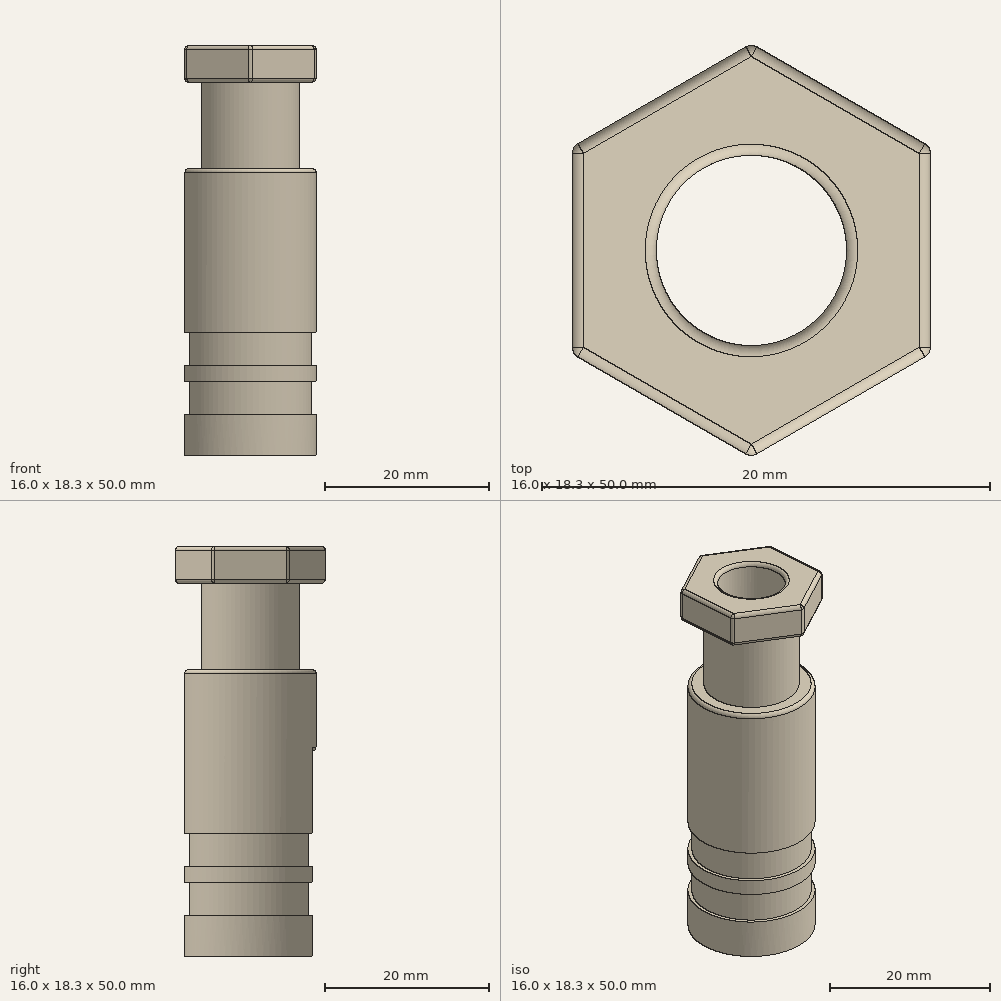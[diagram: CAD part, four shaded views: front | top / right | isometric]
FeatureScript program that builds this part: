
annotation { "Feature Type Name" : "Feature", "Feature Type Description" : "" }
export const myFeature = defineFeature(function(context is Context, id is Id, definition is map)
    precondition{}
    {
        {
            assignVariable(context, id + "F0", {"name" : "Sensor_Laenge", "anyValue" : 25});
        }
        {
            assignVariable(context, id + "F1", {"name" : "Hoehe_Mutter", "anyValue" : 4.5});
        }
        {
            assignVariable(context, id + "F2", {"name" : "Hoehe_Verlaengerung", "anyValue" : 15});
        }
        {
            var Q0;
            Q0=qCreatedBy(makeId("Top.planeOp"),FACE);
            var sketch = newSketch(context, id + "F3", { "sketchPlane" : qUnion([Q0])});
            skLineSegment(sketch, "E0", {"start": v(-2.5, 7.6) * mm, "end": v(-2.5, 3.44) * mm});
            skLineSegment(sketch, "E1", {"start": v(2.5, 7.6) * mm, "end": v(2.5, 3.44) * mm});
            skCircle(sketch, "E2", {"center": v(0, 0) * mm, "radius": 4.25 * mm});
            skCircle(sketch, "E3", {"center": v(0, 0) * mm, "radius": 8 * mm});
            skLineSegment(sketch, "E4", {"start": v(0, 0) * mm, "end": v(0, 8) * mm, "construction": true});
            skCircle(sketch, "E5", {"center": v(0, 0) * mm, "radius": 7.5 * mm});
            skSolve(sketch);
        }
        {
            var Q0;
            {var subQ0=sQuery(id+"F3.wireOp",EDGE,"E2");var subQ1=sQuery(id+"F3.wireOp",EDGE,"E0");var subQ2=makeQuery(id+"F3.imprint","INTERSECT",VERTEX,{"derivedFrom":[subQ1,subQ0]});Q0=makeQuery(id+"F3.imprint","IMPRINT",FACE,{"disambiguationData":[TD([[makeQuery(id+"F3.imprint","IMPRINT",EDGE,{"disambiguationData":[TD([[subQ2,1.0]])],"derivedFrom":subQ1}),-1.0]])]});}
            var Q1;
            {var subQ0=sQuery(id+"F3.wireOp",EDGE,"E3");var subQ1=sQuery(id+"F3.wireOp",EDGE,"E0");var subQ2=makeQuery(id+"F3.imprint","INTERSECT",VERTEX,{"derivedFrom":[subQ1,subQ0]});Q1=makeQuery(id+"F3.imprint","IMPRINT",FACE,{"disambiguationData":[TD([[makeQuery(id+"F3.imprint","IMPRINT",EDGE,{"disambiguationData":[TD([[subQ2,-1.0]])],"derivedFrom":subQ1}),-1.0]])]});}
            extrude(context, id + "F4", {"entities" : qUnion([Q0, Q1]), "oppositeDirection" : true, "depth" : (getVariable(context, 'Sensor_Laenge')) * mm, "offsetDistance" : 25 * mm});
        }
        {
            var Q0;
            {var subQ0=sQuery(id+"F3.wireOp",EDGE,"7UpqIU3J-aBD8-OsaK-lXAZ-pH7eXoIEcfKO.right");var subQ3=sQuery(id+"F3.wireOp",EDGE,"E2");var subQ4=makeQuery(id+"F3.imprint","INTERSECT",VERTEX,{"disambiguationData":[OD(0.0)],"derivedFrom":[subQ3,subQ0]});Q0=makeQuery(id+"F3.imprint","IMPRINT",FACE,{"disambiguationData":[TD([[makeQuery(id+"F3.imprint","IMPRINT",EDGE,{"disambiguationData":[TD([[subQ4,-1.0]])],"derivedFrom":subQ3}),-1.0]])]});}
            var Q1;
            {var subQ0=sQuery(id+"F3.wireOp",EDGE,"E1");Q1=makeQuery(id+"F3.imprint","IMPRINT",FACE,{"disambiguationData":[TD([[makeQuery(id+"F3.imprint","IMPRINT",EDGE,{"derivedFrom":subQ0}),1.0]])]});}
            var Q2;
            {var subQ0=sQuery(id+"F3.wireOp",EDGE,"E1");Q2=makeQuery(id+"F3.imprint","IMPRINT",FACE,{"disambiguationData":[TD([[makeQuery(id+"F3.imprint","IMPRINT",EDGE,{"derivedFrom":subQ0}),-1.0]])]});}
            extrude(context, id + "F5", {"entities" : qUnion([Q0, Q1, Q2]), "operationType" : NewBodyOperationType.ADD, "depth" : 10 * mm, "offsetDistance" : 25 * mm});
        }
        {
            var Q0;
            {var subQ0=sQuery(id+"F3.wireOp",EDGE,"E3");var subQ1=sQuery(id+"F3.wireOp",EDGE,"E0");var subQ2=makeQuery(id+"F3.imprint","INTERSECT",VERTEX,{"derivedFrom":[subQ1,subQ0]});Q0=makeQuery(id+"F3.imprint","IMPRINT",FACE,{"disambiguationData":[TD([[makeQuery(id+"F3.imprint","IMPRINT",EDGE,{"disambiguationData":[TD([[subQ2,-1.0]])],"derivedFrom":subQ1}),-1.0]])]});}
            extrude(context, id + "F6", {"entities" : qUnion([Q0]), "operationType" : NewBodyOperationType.REMOVE, "oppositeDirection" : true, "depth" : 14 * mm, "offsetDistance" : 25 * mm, "hasSecondDirection" : true, "secondDirectionOppositeDirection" : true, "secondDirectionDepth" : 10 * mm});
        }
        {
            var Q0;
            {var subQ0=sQuery(id+"F3.wireOp",EDGE,"E3");var subQ1=sQuery(id+"F3.wireOp",EDGE,"E0");var subQ2=makeQuery(id+"F3.imprint","INTERSECT",VERTEX,{"derivedFrom":[subQ1,subQ0]});Q0=makeQuery(id+"F3.imprint","IMPRINT",FACE,{"disambiguationData":[TD([[makeQuery(id+"F3.imprint","IMPRINT",EDGE,{"disambiguationData":[TD([[subQ2,-1.0]])],"derivedFrom":subQ1}),-1.0]])]});}
            extrude(context, id + "F7", {"entities" : qUnion([Q0]), "operationType" : NewBodyOperationType.REMOVE, "oppositeDirection" : true, "depth" : 20 * mm, "offsetDistance" : 25 * mm, "hasSecondDirection" : true, "secondDirectionOppositeDirection" : true, "secondDirectionDepth" : 16 * mm});
        }
        {
            var Q0;
            Q0=makeQuery(id+"F5.opExtrude","CAP_FACE",FACE,{"disambiguationData":[OSD([sQuery(id+"F3.wireOp",EDGE,"E3"),sQuery(id+"F3.wireOp",EDGE,"WfVQaAh2-LhFR-lcju-hiQk-xBlA84VSb2D0")])],"isStart":false});
            var sketch = newSketch(context, id + "F8", { "sketchPlane" : qUnion([Q0]), "disableImprinting" : false});
            skCircle(sketch, "E6", {"center": v(0, 0) * mm, "radius": 6 * mm});
            skCircle(sketch, "E7", {"center": v(0, 0) * mm, "radius": 4.25 * mm});
            skSolve(sketch);
        }
        {
            var Q0;
            Q0=makeQuery(id+"F8.imprint","IMPRINT",FACE,{"disambiguationData":[TD([[makeQuery(id+"F8.imprint","IMPRINT",EDGE,{"derivedFrom":sQuery(id+"F8.wireOp",EDGE,"E6")}),1.0]])]});
            extrude(context, id + "F9", {"entities" : qUnion([Q0]), "operationType" : NewBodyOperationType.ADD, "depth" : (getVariable(context, 'Hoehe_Verlaengerung')) * mm, "offsetDistance" : 25 * mm});
        }
        {
            var Q0;
            Q0=makeQuery(id+"F9.opExtrude","CAP_FACE",FACE,{"disambiguationData":[OSD([sQuery(id+"F3.wireOp",EDGE,"WfVQaAh2-LhFR-lcju-hiQk-xBlA84VSb2D0"),sQuery(id+"F8.wireOp",EDGE,"E6")])],"isStart":false});
            var sketch = newSketch(context, id + "F10", { "sketchPlane" : qUnion([Q0])});
            skCircle(sketch, "E8", {"center": v(0, 0) * mm, "radius": 2.5 * mm});
            skCircle(sketch, "E9.cCircle", {"center": v(0, 0) * mm, "radius": 8 * mm, "construction": true});
            skLineSegment(sketch, "E9.0", {"start": v(8, 4.62) * mm, "end": v(8, -4.62) * mm});
            skLineSegment(sketch, "E9.1", {"start": v(8, -4.62) * mm, "end": v(0, -9.24) * mm});
            skLineSegment(sketch, "E9.2", {"start": v(0, -9.24) * mm, "end": v(-8, -4.62) * mm});
            skLineSegment(sketch, "E9.3", {"start": v(-8, -4.62) * mm, "end": v(-8, 4.62) * mm});
            skLineSegment(sketch, "E9.4", {"start": v(-8, 4.62) * mm, "end": v(0, 9.24) * mm});
            skLineSegment(sketch, "E9.5", {"start": v(0, 9.24) * mm, "end": v(8, 4.62) * mm});
            skPoint(sketch, "E9.0.midPoint", {"position": v(8, 0) * mm});
            skCircle(sketch, "E10", {"center": v(0, 0) * mm, "radius": 6 * mm});
            skSolve(sketch);
        }
        {
            var Q0;
            Q0=makeQuery(id+"F10.imprint","IMPRINT",FACE,{"disambiguationData":[TD([[makeQuery(id+"F10.imprint","IMPRINT",EDGE,{"derivedFrom":sQuery(id+"F10.wireOp",EDGE,"E9.0")}),-1.0]])]});
            extrude(context, id + "F11", {"entities" : qUnion([Q0]), "operationType" : NewBodyOperationType.ADD, "oppositeDirection" : true, "depth" : (getVariable(context, 'Hoehe_Mutter')) * mm, "offsetDistance" : 25 * mm});
        }
        {
            var Q0;
            Q0=makeQuery(id+"F10.imprint","IMPRINT",FACE,{"disambiguationData":[TD([[makeQuery(id+"F10.imprint","IMPRINT",EDGE,{"derivedFrom":sQuery(id+"F10.wireOp",EDGE,"E10")}),-1.0]])]});
            extrude(context, id + "F12", {"entities" : qUnion([Q0]), "operationType" : NewBodyOperationType.REMOVE, "oppositeDirection" : true, "depth" : 10 * mm, "offsetDistance" : 25 * mm, "hasSecondDirection" : true, "secondDirectionOppositeDirection" : true, "secondDirectionDepth" : 6 * mm});
        }
        {
            var Q0;
            Q0=makeQuery(id+"F9.opExtrude","CAP_EDGE",EDGE,{"disambiguationData":[OSD([sQuery(id+"F8.wireOp",EDGE,"E7")])],"isStart":false});
            var Q1;
            Q1=makeQuery(id+"F11.opExtrude","SWEPT_FACE",FACE,{"disambiguationData":[OSD([sQuery(id+"F10.wireOp",EDGE,"E9.0")])]});
            var Q2;
            Q2=makeQuery(id+"F11.opExtrude","SWEPT_FACE",FACE,{"disambiguationData":[OSD([sQuery(id+"F10.wireOp",EDGE,"E9.1")])]});
            var Q3;
            Q3=makeQuery(id+"F11.opExtrude","SWEPT_FACE",FACE,{"disambiguationData":[OSD([sQuery(id+"F10.wireOp",EDGE,"E9.5")])]});
            var Q4;
            Q4=makeQuery(id+"F11.opExtrude","SWEPT_FACE",FACE,{"disambiguationData":[OSD([sQuery(id+"F10.wireOp",EDGE,"E9.4")])]});
            var Q5;
            Q5=makeQuery(id+"F11.opExtrude","SWEPT_FACE",FACE,{"disambiguationData":[OSD([sQuery(id+"F10.wireOp",EDGE,"E9.3")])]});
            var Q6;
            Q6=makeQuery(id+"F11.opExtrude","SWEPT_FACE",FACE,{"disambiguationData":[OSD([sQuery(id+"F10.wireOp",EDGE,"E9.2")])]});
            var Q7;
            Q7=makeQuery(id+"F5.opExtrude","CAP_EDGE",EDGE,{"disambiguationData":[OSD([sQuery(id+"F3.wireOp",EDGE,"E3")])],"isStart":false});
            var Q8;
            Q8=makeQuery(id+"F12.boolean.opBoolean","COPY",EDGE,{"derivedFrom":makeQuery(id+"F12.opExtrude","CAP_EDGE",EDGE,{"disambiguationData":[OSD([sQuery(id+"F8.wireOp",EDGE,"E6")])],"isStart":true})});
            var Q9;
            Q9=makeQuery(id+"F6.boolean.opBoolean","COPY",EDGE,{"derivedFrom":makeQuery(id+"F6.opExtrude","CAP_EDGE",EDGE,{"disambiguationData":[OSD([sQuery(id+"F3.wireOp",EDGE,"E3")])],"isStart":true})});
            var Q10;
            Q10=makeQuery(id+"F7.boolean.opBoolean","COPY",EDGE,{"derivedFrom":makeQuery(id+"F7.opExtrude","CAP_EDGE",EDGE,{"disambiguationData":[OSD([sQuery(id+"F3.wireOp",EDGE,"E3")])],"isStart":true})});
            var Q11;
            Q11=makeQuery(id+"F6.boolean.opBoolean","COPY",EDGE,{"derivedFrom":makeQuery(id+"F6.opExtrude","CAP_EDGE",EDGE,{"disambiguationData":[OSD([sQuery(id+"F3.wireOp",EDGE,"E3")])],"isStart":false})});
            var Q12;
            Q12=makeQuery(id+"F4.opExtrude","CAP_EDGE",EDGE,{"disambiguationData":[OSD([sQuery(id+"F3.wireOp",EDGE,"E2")])],"isStart":false});
            var Q13;
            Q13=makeQuery(id+"F4.opExtrude","CAP_EDGE",EDGE,{"disambiguationData":[OSD([sQuery(id+"F3.wireOp",EDGE,"E1")])],"isStart":false});
            var Q14;
            Q14=makeQuery(id+"F4.opExtrude","CAP_EDGE",EDGE,{"disambiguationData":[OSD([sQuery(id+"F3.wireOp",EDGE,"E0")])],"isStart":false});
            var Q15;
            Q15=makeQuery(id+"F5.opExtrude","CAP_EDGE",EDGE,{"disambiguationData":[OSD([sQuery(id+"F3.wireOp",EDGE,"E3")])],"isStart":true});
            var Q16;
            Q16=makeQuery(id+"F7.boolean.opBoolean","COPY",EDGE,{"derivedFrom":makeQuery(id+"F7.opExtrude","CAP_EDGE",EDGE,{"disambiguationData":[OSD([sQuery(id+"F3.wireOp",EDGE,"E3")])],"isStart":false})});
            fillet(context, id + "F13", {"entities" : qUnion([Q0, Q1, Q2, Q3, Q4, Q5, Q6, Q7, Q8, Q9, Q10, Q11, Q12, Q13, Q14, Q15, Q16]), "radius" : 0.5 * mm, "tangentPropagation" : true, "allowEdgeOverflow" : false});
        }
    });
